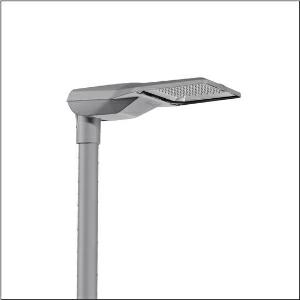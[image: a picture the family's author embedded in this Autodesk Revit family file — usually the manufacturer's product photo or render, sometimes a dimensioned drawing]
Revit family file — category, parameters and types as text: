
# Revit family: streetlight_sl_21_midi___stw1_0a_5xe7e33a08mb_c91c
name_source: partatom
category: Lighting Fixtures
units: mm (PartAtom-declared; Revit-internal decimal feet)

## family parameters
Cut with Voids When Loaded = No
Host = Face
Light Source = No
Part Type = Normal
Room Calculation Point = No
Round Connector Dimension = Use Diameter
Shared = No

## types (1)
- --- (1 x LED, 18270 lm, 136 W, 3000K)
    Apparent Load = 136 VA
    CIE Flux Codes = 38 75 98 100 100
    Color Rendering = 70
    Color Temperature = 3000K
    Default Elevation = 1800 mm
    Description = Streetlight SL 21 midi, mast luminaire, primary light control with lens, of PMMA, primary optical cover: cover, of toughened safety glass, transparent, light distribution: STW1.0a, light emission: direct distribution, primary light characteristic: asymmetric, installation type: post-top, side-entry, LED, 3G 1.5mm², High Power LED, rated luminous flux: 18.270lm, luminous efficacy: 134lm/W, light colour: 730, colour temperature: 3000K, control: overheat protection, constant luminous flux control, time-dependent luminous flux control, flexible luminous flux parameterisation, mains connection: 220..240V, AC, 50/60Hz, connection cable pre-assembled, cable length: 12,5m, wiring characteristics: H07RN-F, start of lifetime: 136W, end of service life: 142W, reduction: 61W, luminaire housing, of diecast aluminium, powder-coated, Siteco® metallic grey (DB 702S), corrosivity category C5 mid according to DIN EN ISO 12944, please order mast flange separately, inclination adjustable: 0°, 5°, 10°, 15°, sealing non-destructively replaceable, multi-level sealing system, length: 644mm, width: 335mm, height: 110mm, mast flange for spigot size: 42mm (side-entry): 5XC10008XM4, 60/48mm (side-entry/post-top): 5XC10108XM2, 76/60mm (side-entry/post-top): 5XC10108XM1, protection rating (complete): IP66, insulation class (complete): insulation class II (safety insulation), certification: CE, ENEC, ENEC+, VDE, impact resistance: IK09, permissible operating ambient temperature for outdoor applications: -40..+50°C, standard-compliant lighting for roads and squares, packaging unit: 1 piece

Light Distribution: STW1.0a
    Height = 111 mm
    Lamp = 1 x LED
    Lamp Light Flux = 18270 lm
    Lamp Power = 136 W
    Lamp count = 1
    Length = 644 mm
    Luminous efficacy = 134 lm/W
    Manufacturer = Siteco
    ModVariant = No
    Model = 5XE7E33A08MB
    Number of Poles = 1
    OnlyDefault = Yes
    Power Factor = 1
    Product Name = Streetlight SL 21 midi | STW1.0a
    Product group = mast luminaire | pylon top
    ProductGroupID = 6100
    Protection Class = Protection class II
    Protection Degree = IP 66
    RLX_Detail_Level = 1
    RLX_Emergency_Light_Flux = 0 lm
    RLX_Emergency_Type = 0
    RLX_Emergency_Type_DB = No
    RlxData = <blob elided: 90393 chars, md5=3fbbdfee>
    Socket = socket
    Standby Power = 0 W
    System Light Flux = 18270 lm
    System Power = 136 W
    Type Comments = factory setting: luminous flux: 100 % | Output Level: 100 % | 695 mA
    Type Image = l_1004298.jpg
    URL = http://relux.com
    VarID = @adj_121171
    Voltage = 0 V
    Weight = 0.00 kg
    Width = 336 mm

## geometry (parser evidence)
native form markers: Blend x4, Sweep x10
no freeform markers — native parametric forms only
